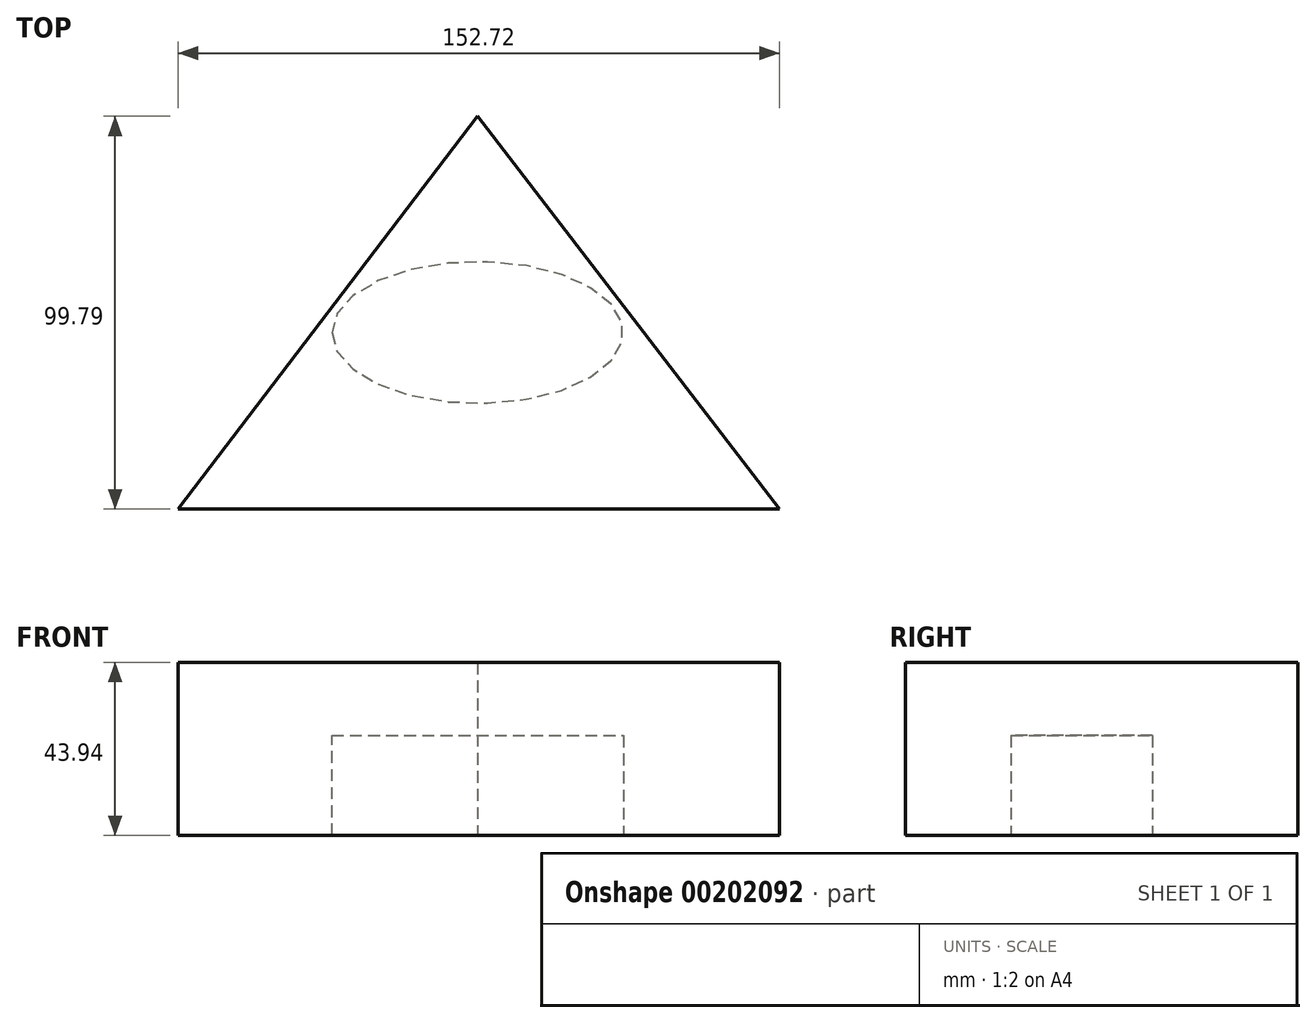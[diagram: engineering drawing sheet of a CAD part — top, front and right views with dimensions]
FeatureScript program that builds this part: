
annotation { "Feature Type Name" : "Feature", "Feature Type Description" : "" }
export const myFeature = defineFeature(function(context is Context, id is Id, definition is map)
    precondition{}
    {
        {
            var Q0;
            Q0=qCreatedBy(makeId("Top.planeOp"),FACE);
            var sketch = newSketch(context, id + "F0", { "sketchPlane" : qUnion([Q0])});
            skLineSegment(sketch, "E0", {"start": v(-76.07, -24.15) * mm, "end": v(76.65, -24.15) * mm});
            skLineSegment(sketch, "E1", {"start": v(-76.07, -24.15) * mm, "end": v(0, 75.64) * mm});
            skLineSegment(sketch, "E2", {"start": v(0, 75.64) * mm, "end": v(76.65, -24.15) * mm});
            skSolve(sketch);
        }
        {
            var Q0;
            Q0 = qSketchRegion(id + "F0", true);
            extrude(context, id + "F1", {"entities" : qUnion([Q0]), "depth" : 43.94 * mm});
        }
        {
            var Q0;
            Q0=qCreatedBy(makeId("Top.planeOp"),FACE);
            cPlane(context, id + "F2", {"entities" : qUnion([Q0]), "cplaneType" : CPlaneType.OFFSET, "offset" : 25.4 * mm, "width" : 152.4 * mm, "height" : 152.4 * mm});
        }
        {
            var Q0;
            Q0=qCreatedBy(id+"F2.planeOp",FACE);
            var sketch = newSketch(context, id + "F3", { "sketchPlane" : qUnion([Q0])});
            skEllipse(sketch, "E3", {"center": v(0, 20.68) * mm, "majorRadius": 37.02 * mm, "minorRadius": 17.99 * mm, "majorAxis": v(-1, 0)});
            skSolve(sketch);
        }
        {
            var Q0;
            Q0 = qSketchRegion(id + "F3", true);
            extrude(context, id + "F4", {"entities" : qUnion([Q0]), "operationType" : NewBodyOperationType.REMOVE, "oppositeDirection" : true, "depth" : 254 * mm});
        }
    });
